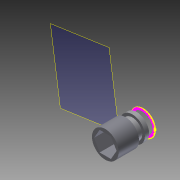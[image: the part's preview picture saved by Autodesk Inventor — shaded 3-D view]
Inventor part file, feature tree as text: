
AUTODESK INVENTOR PART (.ipt)
format: ipt  version: 2012 (Build 160160000, 160)  size: 171,008 bytes
history: native  units: in
note: dims shown in document units (in); Inventor stores cm internally (conversion verified against a paired STEP export)
features: extrude x4, sketch x4, other x3
ambient origin geometry x8: Origin, YZ Plane, XZ Plane, XY Plane, X Axis, Y Axis, Z Axis, Center Point
bodies: Solid1 (feature_tree)
feature tree (11):
  other  "Spur Gear1"
  extrude  "Extrusion1"  Depth=0.6264in
  extrude  "Extrusion2"  Depth=0.3937in TaperAngle=0.0deg
  extrude  "Extrusion3"  Depth=0.4921in
  extrude  "Extrusion4"  Depth=0.1575in TaperAngle=0.0deg
  other  "Solid1::Spur Gear1"
  other  "TaggingFeature1"
  sketch  "Sketch3"  dims[d0=0.3937in d1=0.6264in]
  sketch  "Sketch4"  dims[d2=1.0in d3=0.0in d4=0.3937in d5=0.0in]
  sketch  "Sketch5"  dims[d6=0.1969in d7=0.4921in]
  sketch  "Sketch6"  dims[d8=0.3937in d9=0.0in d10=0.1575in d11=0.0in]
